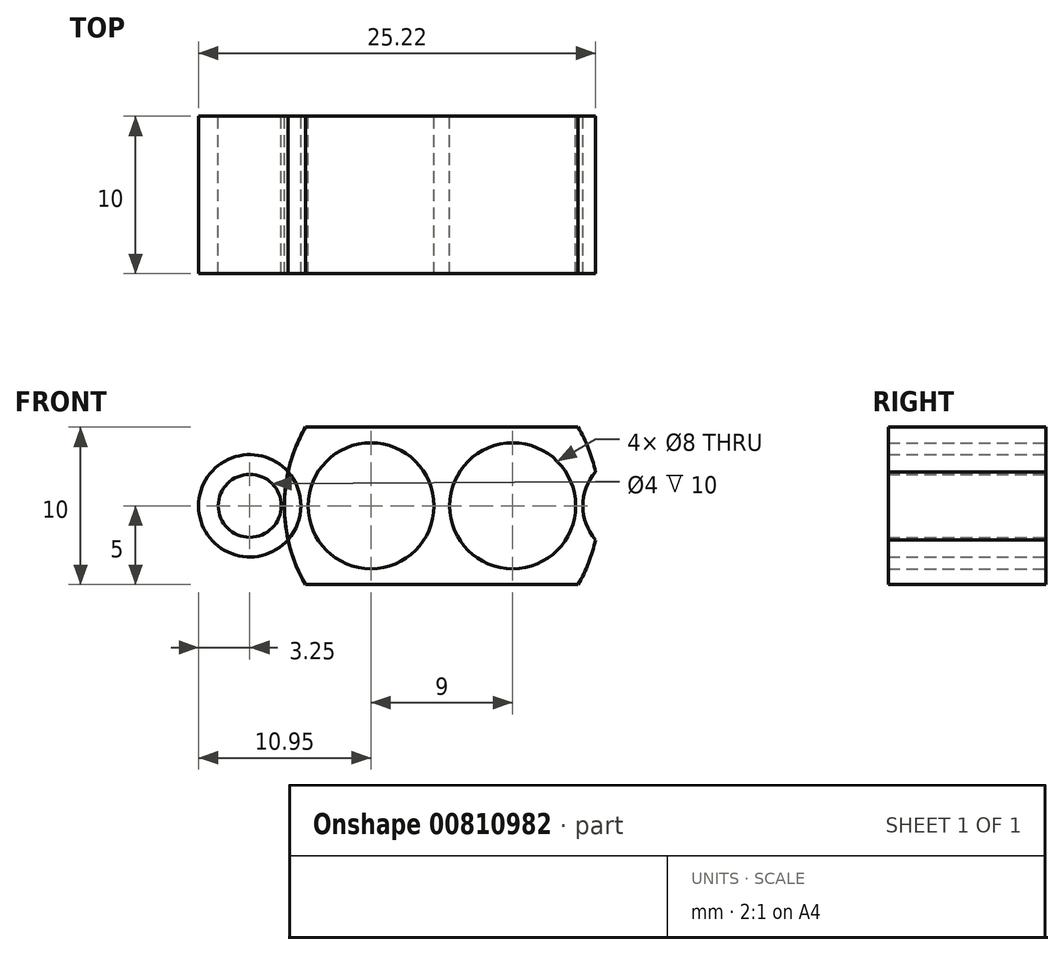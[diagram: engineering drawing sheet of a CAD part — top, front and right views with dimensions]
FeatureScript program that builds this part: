
annotation { "Feature Type Name" : "Feature", "Feature Type Description" : "" }
export const myFeature = defineFeature(function(context is Context, id is Id, definition is map)
    precondition{}
    {
        {
            var Q0;
            Q0=qCreatedBy(makeId("Front.planeOp"),FACE);
            var sketch = newSketch(context, id + "F0", { "sketchPlane" : qUnion([Q0])});
            skCircle(sketch, "E0", {"center": v(0, 0) * mm, "radius": 10 * mm});
            skCircle(sketch, "E1", {"center": v(-4.5, 0) * mm, "radius": 4 * mm});
            skCircle(sketch, "E2", {"center": v(4.5, 0) * mm, "radius": 4 * mm});
            skCircle(sketch, "E3", {"center": v(-12.2, 0) * mm, "radius": 3.25 * mm});
            skCircle(sketch, "E4", {"center": v(-12.2, 0) * mm, "radius": 2 * mm});
            skCircle(sketch, "E5", {"center": v(12.2, 0) * mm, "radius": 3.25 * mm});
            skCircle(sketch, "E6", {"center": v(12.2, 0) * mm, "radius": 2 * mm});
            skLineSegment(sketch, "E7.bottom", {"start": v(12.35, 5) * mm, "end": v(11.35, 5) * mm});
            skLineSegment(sketch, "E7.top", {"start": v(12.35, 15) * mm, "end": v(-12.35, 15) * mm});
            skLineSegment(sketch, "E7.left", {"start": v(12.35, 5) * mm, "end": v(12.35, 15) * mm});
            skLineSegment(sketch, "E7.right", {"start": v(-12.35, 5) * mm, "end": v(-12.35, 15) * mm});
            skPoint(sketch, "E7.middle", {"position": v(0, 10) * mm});
            skLineSegment(sketch, "E8.bottom", {"start": v(13.02, -5) * mm, "end": v(-13.02, -5) * mm});
            skLineSegment(sketch, "E8.top", {"start": v(13.02, -15) * mm, "end": v(-13.02, -15) * mm});
            skLineSegment(sketch, "E8.left", {"start": v(13.02, -5) * mm, "end": v(13.02, -15) * mm});
            skLineSegment(sketch, "E8.right", {"start": v(-13.02, -5) * mm, "end": v(-13.02, -15) * mm});
            skPoint(sketch, "E8.middle", {"position": v(0, -10) * mm});
            skLineSegment(sketch, "E9", {"start": v(11.35, 5) * mm, "end": v(-10.12, 5) * mm});
            skLineSegment(sketch, "E10", {"start": v(-10.12, 5) * mm, "end": v(-12.35, 5) * mm});
            skSolve(sketch);
        }
        {
            var Q0;
            Q0=makeQuery(id+"F0.imprint","IMPRINT",FACE,{"disambiguationData":[TD([[makeQuery(id+"F0.imprint","IMPRINT",EDGE,{"derivedFrom":sQuery(id+"F0.wireOp",EDGE,"E0")}),1.0]])]});
            extrude(context, id + "F1", {"entities" : qUnion([Q0]), "depth" : 10 * mm, "offsetDistance" : 25 * mm});
        }
        {
            var Q0;
            {var subQ0=sQuery(id+"F0.wireOp",EDGE,"E3");var subQ1=sQuery(id+"F0.wireOp",EDGE,"E0");var subQ2=makeQuery(id+"F0.imprint","INTERSECT",VERTEX,{"disambiguationData":[OD(0.0)],"derivedFrom":[subQ1,subQ0]});Q0=makeQuery(id+"F0.imprint","IMPRINT",FACE,{"disambiguationData":[TD([[makeQuery(id+"F0.imprint","IMPRINT",EDGE,{"disambiguationData":[TD([[subQ2,-1.0]])],"derivedFrom":subQ1}),-1.0]])]});}
            var Q1;
            {var subQ0=sQuery(id+"F0.wireOp",EDGE,"E5");var subQ1=sQuery(id+"F0.wireOp",EDGE,"E0");var subQ2=makeQuery(id+"F0.imprint","INTERSECT",VERTEX,{"disambiguationData":[OD(0.0)],"derivedFrom":[subQ1,subQ0]});Q1=makeQuery(id+"F0.imprint","IMPRINT",FACE,{"disambiguationData":[TD([[makeQuery(id+"F0.imprint","IMPRINT",EDGE,{"disambiguationData":[TD([[subQ2,1.0]])],"derivedFrom":subQ1}),-1.0]])]});}
            extrude(context, id + "F2", {"entities" : qUnion([Q0, Q1]), "depth" : 10 * mm, "offsetDistance" : 25 * mm});
        }
        {
            var Q0;
            {var subQ0=sQuery(id+"F0.wireOp",EDGE,"E5");var subQ1=sQuery(id+"F0.wireOp",EDGE,"E0");var subQ2=makeQuery(id+"F0.imprint","INTERSECT",VERTEX,{"disambiguationData":[OD(0.0)],"derivedFrom":[subQ1,subQ0]});Q0=makeQuery(id+"F0.imprint","IMPRINT",FACE,{"disambiguationData":[TD([[makeQuery(id+"F0.imprint","IMPRINT",EDGE,{"disambiguationData":[TD([[subQ2,1.0]])],"derivedFrom":subQ1}),1.0]])]});}
            var Q1;
            {var subQ0=sQuery(id+"F0.wireOp",EDGE,"E3");var subQ1=sQuery(id+"F0.wireOp",EDGE,"E0");var subQ2=makeQuery(id+"F0.imprint","INTERSECT",VERTEX,{"disambiguationData":[OD(0.0)],"derivedFrom":[subQ1,subQ0]});Q1=makeQuery(id+"F0.imprint","IMPRINT",FACE,{"disambiguationData":[TD([[makeQuery(id+"F0.imprint","IMPRINT",EDGE,{"disambiguationData":[TD([[subQ2,-1.0]])],"derivedFrom":subQ1}),1.0]])]});}
            extrude(context, id + "F3", {"entities" : qUnion([Q0, Q1]), "depth" : 10 * mm, "offsetDistance" : 25 * mm});
        }
    });
